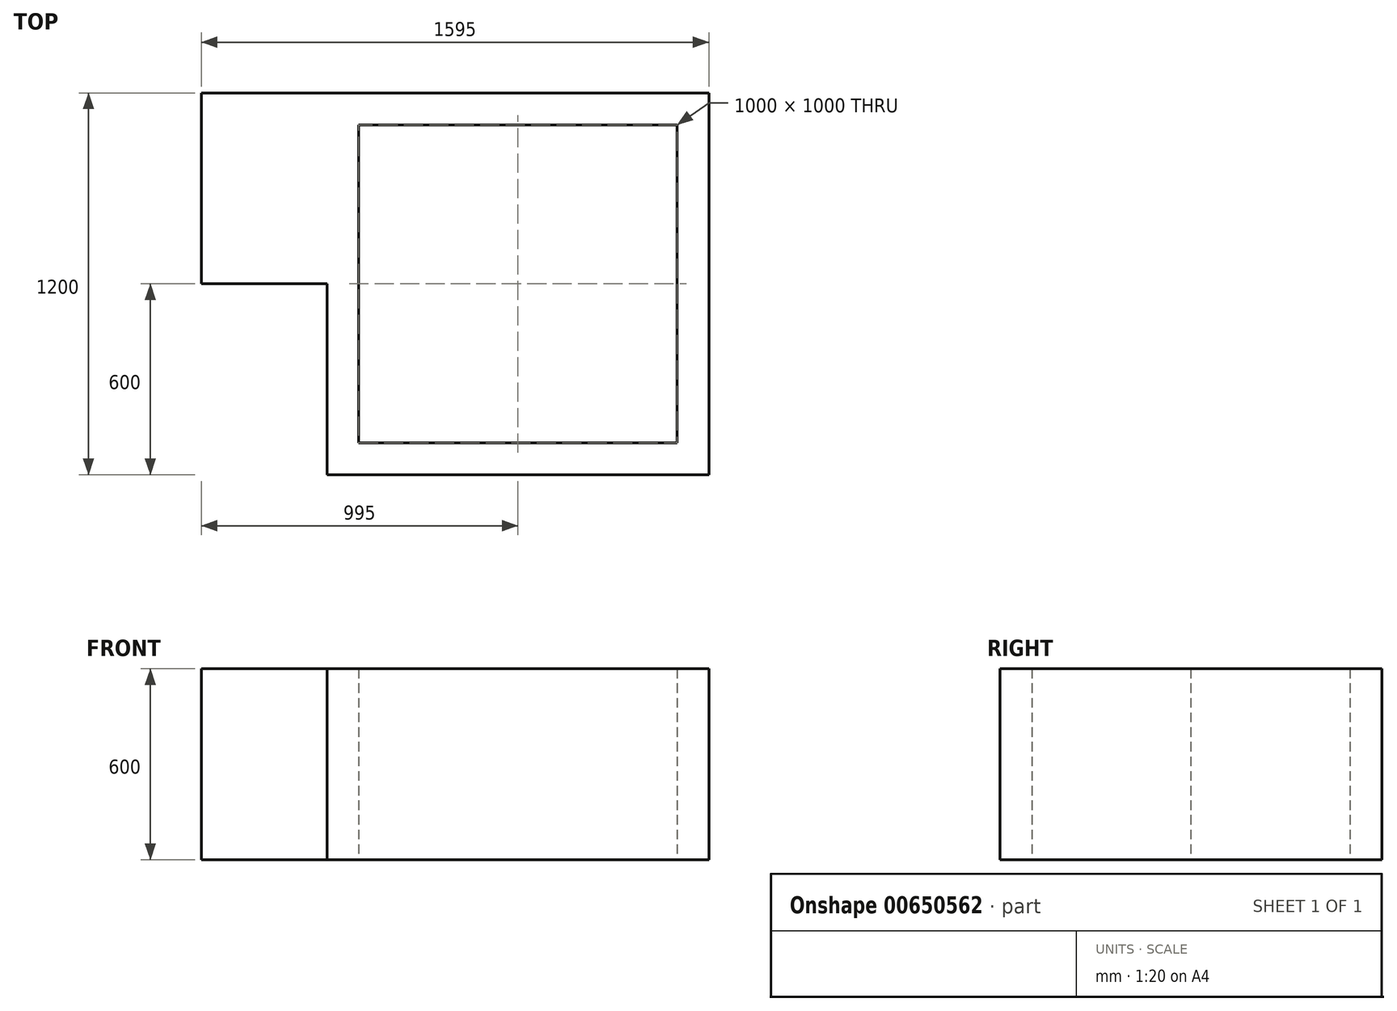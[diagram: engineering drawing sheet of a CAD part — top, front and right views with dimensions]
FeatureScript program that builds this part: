
annotation { "Feature Type Name" : "Feature", "Feature Type Description" : "" }
export const myFeature = defineFeature(function(context is Context, id is Id, definition is map)
    precondition{}
    {
        {
            var Q0;
            Q0=qCreatedBy(makeId("Top.planeOp"),FACE);
            var sketch = newSketch(context, id + "F0", { "sketchPlane" : qUnion([Q0])});
            skLineSegment(sketch, "E0.bottom", {"start": v(0, 0) * mm, "end": v(-1200, 0) * mm});
            skLineSegment(sketch, "E0.top", {"start": v(0, 1200) * mm, "end": v(-1595, 1200) * mm});
            skLineSegment(sketch, "E0.left", {"start": v(0, 0) * mm, "end": v(0, 1200) * mm});
            skLineSegment(sketch, "E1", {"start": v(-1595, 1200) * mm, "end": v(-1595, 600) * mm});
            skLineSegment(sketch, "E2", {"start": v(-1595, 600) * mm, "end": v(-1200, 600) * mm});
            skLineSegment(sketch, "E3", {"start": v(-1200, 600) * mm, "end": v(-1200, 0) * mm});
            skLineSegment(sketch, "E4.bottom", {"start": v(-100, 100) * mm, "end": v(-1100, 100) * mm});
            skLineSegment(sketch, "E4.top", {"start": v(-100, 1100) * mm, "end": v(-1100, 1100) * mm});
            skLineSegment(sketch, "E4.left", {"start": v(-100, 100) * mm, "end": v(-100, 1100) * mm});
            skLineSegment(sketch, "E4.right", {"start": v(-1100, 100) * mm, "end": v(-1100, 1100) * mm});
            skSolve(sketch);
        }
        {
            var Q0;
            Q0=qSketchRegion(id+"F0",true);
            extrude(context, id + "F1", {"entities" : qUnion([Q0]), "depth" : 600 * mm, "offsetDistance" : 25 * mm});
        }
    });
